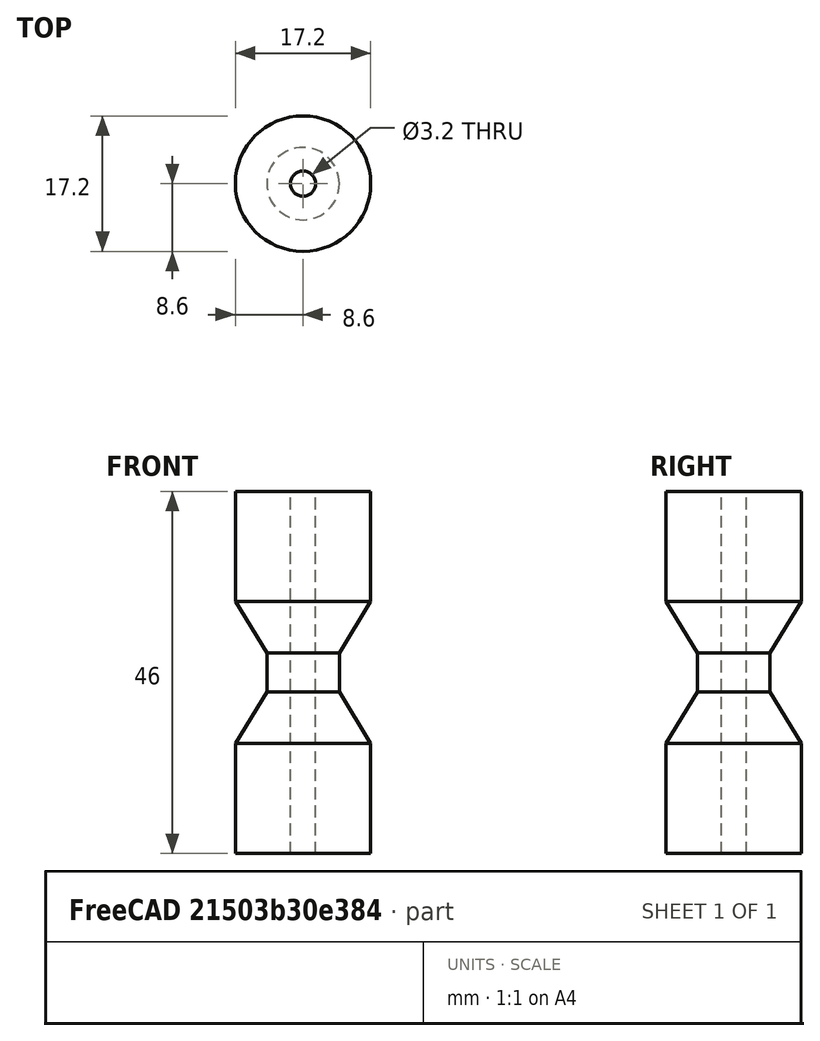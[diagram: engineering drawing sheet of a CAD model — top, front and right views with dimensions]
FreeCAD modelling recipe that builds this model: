
FCSTD DOCUMENT  (FreeCAD 1.0R39109 (Git))
Label: roller_centring_MK2
License: All rights reserved
LicenseURL: http://en.wikipedia.org/wiki/All_rights_reserved
objects: Sketcher::SketchObject×1, PartDesign::Revolution×1, PartDesign::Body×1
note: 6 computed .brp shape members not serialized (recipe doc carries the construction recipe); baked Part::Feature solids carry a one-line shape summary decoded from their .brp

FEATURE [Sketcher::SketchObject] Sketch
  ArcFitTolerance = 1e-06
  AttachmentSupport = -> [XZ_Plane]
  FullyConstrained = false
  MakeInternals = false
  MapMode = 5
  Placement = pos=(0,0,0) rot=(1,0,0;1.5708rad)
  sketch-geometry (10):
    g0: LineSegment StartX=1.6 StartY=0 StartZ=0 EndX=1.6 EndY=23 EndZ=0
    g1: LineSegment StartX=1.6 StartY=23 StartZ=0 EndX=8.6 EndY=23 EndZ=0
    g2: LineSegment StartX=8.6 StartY=23 StartZ=0 EndX=8.6 EndY=9 EndZ=0
    g3: LineSegment StartX=8.6 StartY=9 StartZ=0 EndX=4.6 EndY=2.5 EndZ=0
    g4: LineSegment StartX=4.6 StartY=2.5 StartZ=0 EndX=4.6 EndY=0 EndZ=0
    g5: LineSegment StartX=1.6 StartY=0 StartZ=0 EndX=1.6 EndY=-23 EndZ=0
    g6: LineSegment StartX=1.6 StartY=-23 StartZ=0 EndX=8.6 EndY=-23 EndZ=0
    g7: LineSegment StartX=8.6 StartY=-23 StartZ=0 EndX=8.6 EndY=-9 EndZ=0
    g8: LineSegment StartX=8.6 StartY=-9 StartZ=0 EndX=4.6 EndY=-2.5 EndZ=0
    g9: LineSegment StartX=4.6 StartY=-2.5 StartZ=0 EndX=4.6 EndY=0 EndZ=0
  constraints (24):
    c: PointOnObject(g0,g-1)
    c: Vertical(g0)
    c: Coincident(g0,g1)
    c: Horizontal(g1)
    c: Coincident(g1,g2)
    c: Vertical(g2)
    c: Coincident(g2,g3)
    c: Coincident(g3,g4)
    c: Vertical(g4)
    c: DistanceX(g-1,g0) = 1.6
    c: DistanceY(g0,g0) = 23
    c: DistanceY(g4,g4) = 2.5
    c: PointOnObject(g4,g-1)
    c: DistanceX(g1,g1) = 7
    c: DistanceY(g2,g2) = 14
    c: DistanceX(g0,g4) = 3
    c: Vertical(g5)
    c: Coincident(g5,g6)
    c: Horizontal(g6)
    c: Coincident(g6,g7)
    c: Vertical(g7)
    c: Coincident(g7,g8)
    c: Coincident(g8,g9)
    c: Vertical(g9)
FEATURE [PartDesign::Revolution] Revolution
  Angle = 360
  Angle2 = 60
  Axis = (0,2e-16,1)
  Base = (0,0,0)
  Placement = pos=(0,0,0) rot=(1,0,0;1.5708rad)
  Profile = -> Sketch
  ReferenceAxis = -> Sketch [V_Axis]
  Refine = true
  Reversed = true
  Suppressed = false
  Type = 0
FEATURE [PartDesign::Body] Body
  AllowCompound = false
  Group = -> [Sketch,Revolution]
  Origin = -> Origin
  Tip = -> Revolution
